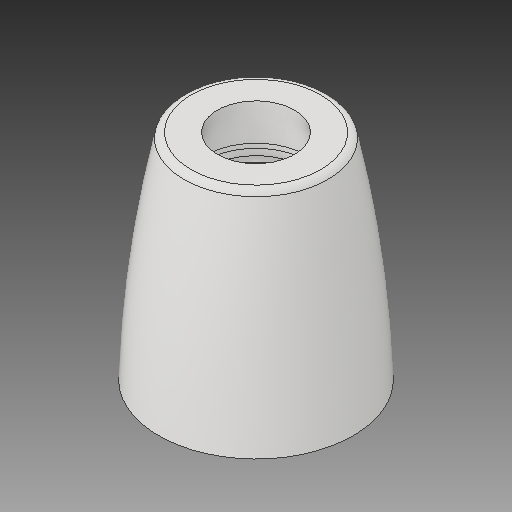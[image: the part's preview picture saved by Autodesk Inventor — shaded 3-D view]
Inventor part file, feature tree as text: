
AUTODESK INVENTOR PART (.ipt)
format: ipt  version: 2019 (Build 230136000, 136)  size: 157,184 bytes
history: native  units: in
note: dims shown in document units (in); Inventor stores cm internally (conversion verified against a paired STEP export)
features: revolve x1
ambient origin geometry x8: Origin, YZ Plane, XZ Plane, XY Plane, X Axis, Y Axis, Z Axis, Center Point
bodies: Solid1 (feature_tree)
feature tree (1):
  revolve  "Revolve1"  [1 undecoded]
note: 1 required parameter value undecoded (feature->parameter linkage not recoverable at this tier; creation-order binding heuristic only, values carry confidence <= 0.55)
